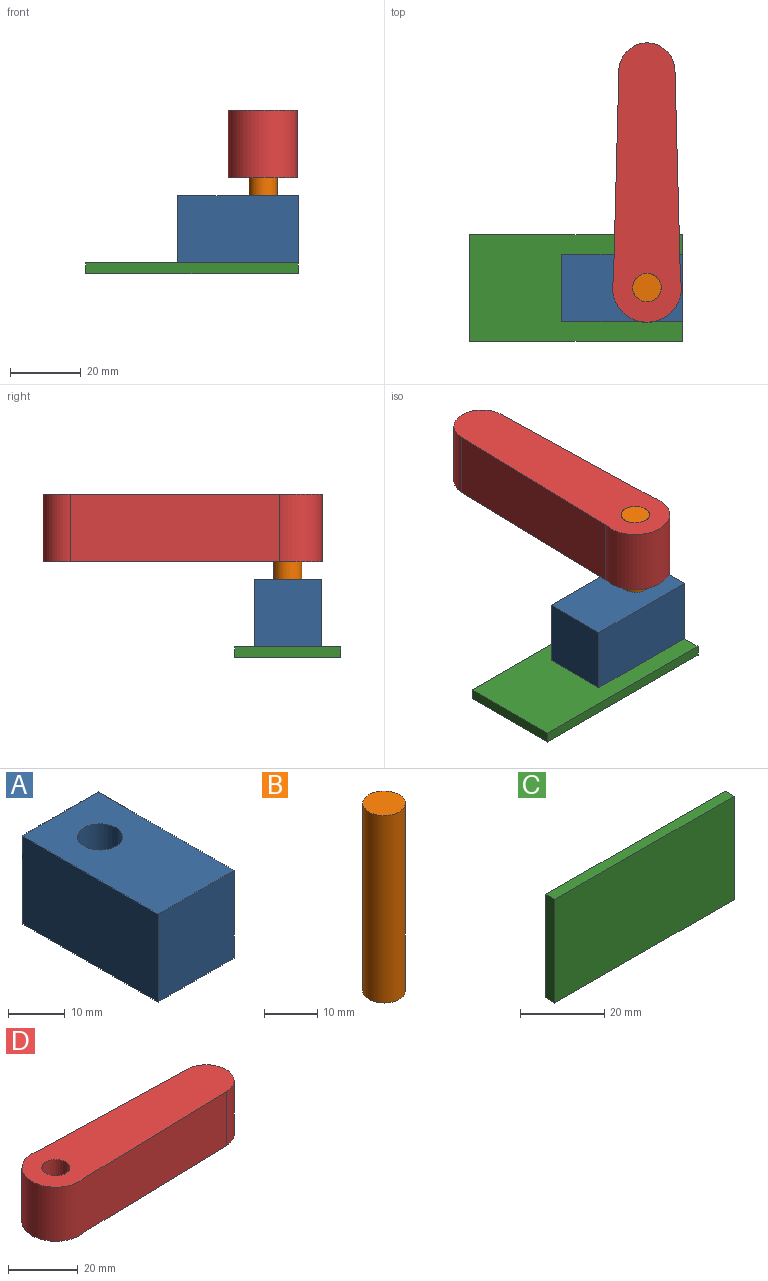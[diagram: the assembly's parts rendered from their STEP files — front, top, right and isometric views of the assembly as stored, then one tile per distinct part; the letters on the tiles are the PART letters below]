
ASSEMBLY  parts=4 mates=3
PART A: 7 faces, bbox 19x34x19 mm
  f0: plane 19x19mm, normal (0,1,0), area 361mm2, adj f1,f3,f4,f5
  f1: plane 34x19mm, normal (-1,0,0), area 646mm2, adj f0,f2,f4,f5
  f2: plane 19x19mm, normal (0,-1,0), area 361mm2, adj f1,f3,f4,f5
  f3: plane 34x19mm, normal (1,0,0), area 646mm2, adj f0,f2,f4,f5
  f4: plane 34x19mm, normal (0,0,1), area 595.7mm2, adj f0,f1,f2,f3,f6
  f5: plane 34x19mm, normal (0,0,-1), area 595.7mm2, adj f0,f1,f2,f3,f6
  f6: cylinder r=4mm len=19mm, axis (0,0,1), area 477.5mm2, adj f4,f5
PART B: 3 faces, bbox 8x8x43 mm
  f0: cylinder r=4mm len=43mm, axis (0,0,-1), area 1080.7mm2, adj f1,f2
  f1: plane 8x8mm, normal (0,0,1), area 50.3mm2, adj f0
  f2: plane 8x8mm, normal (0,0,-1), area 50.3mm2, adj f0
PART C: 6 faces, bbox 60x3x30 mm
  f0: plane 60x3mm, normal (0,0,1), area 180mm2, adj f1,f3,f4,f5
  f1: plane 30x3mm, normal (-1,0,0), area 90mm2, adj f0,f2,f4,f5
  f2: plane 60x3mm, normal (0,0,-1), area 180mm2, adj f1,f3,f4,f5
  f3: plane 30x3mm, normal (1,0,0), area 90mm2, adj f0,f2,f4,f5
  f4: plane 60x30mm, normal (0,-1,0), area 1800mm2, adj f0,f1,f2,f3
  f5: plane 60x30mm, normal (0,1,0), area 1800mm2, adj f0,f1,f2,f3
PART D: 7 faces, bbox 78.8x19.5x19 mm
  f0: cylinder r=7.91mm len=19mm, axis (0,0,-1), area 464.2mm2, adj f1,f3,f5,f6
  f1: plane 58.96x19mm, normal (0.03,1,0), area 1120.6mm2, adj f0,f2,f5,f6
  f2: cylinder r=9.73mm len=19.46mm, axis (0,0,-1), area 671.6mm2, adj f1,f3,f5,f6
  f3: plane 58.96x19mm, normal (0.03,-1,0), area 1120.6mm2, adj f0,f2,f5,f6
  f4: cylinder r=4mm len=19mm, axis (0,0,-1), area 477.5mm2, adj f5,f6
  f5: plane 78.75x19.46mm, normal (0,0,1), area 1261.5mm2, adj f0,f1,f2,f3,f4
  f6: plane 78.75x19.46mm, normal (0,0,-1), area 1261.5mm2, adj f0,f1,f2,f3,f4
PLACE A rot(axis=(0,0,-1),90deg) t=(21.34,9.61,6.93)mm
PLACE B rot(axis=(-1,0,0),180deg) t=(28.34,9.61,49.93)mm
PLACE C rot(axis=(-1,0,0),90deg) t=(8.34,9.61,3.93)mm
PLACE D rot(axis=(0,0,1),90deg) t=(28.34,40.17,30.93)mm
MATE fastened B.f0 <-> A.f6  axis (0,0,-1) through (28.34,9.61,6.93)mm
MATE fastened D.f2 <-> B.f0  axis (0,0,-1) through (28.34,9.61,49.93)mm
MATE fastened A.f5 <-> C.f4  axis (0,0,-1) through (38.34,9.61,6.93)mm
